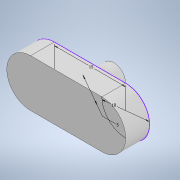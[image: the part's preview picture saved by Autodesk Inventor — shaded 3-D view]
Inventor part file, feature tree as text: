
AUTODESK INVENTOR PART (.ipt)
format: ipt  version: 2022 (Build 260153000, 153)  size: 107,008 bytes
history: native  units: mm
features: extrude x2, sketch x1
ambient origin geometry x8: Origin, YZ Plane, XZ Plane, XY Plane, X Axis, Y Axis, Z Axis, Center Point
bodies: Body1 (feature_tree)
feature tree (3):
  sketch  "Sketch1"  dims[d0=10.0mm d1=5.0mm d7=5.0mm d8=0.0mm d9=5.0mm d10=0.0mm d11=15.0mm]
  extrude  "Extrusion3"  Depth=5.0mm
  extrude  "Extrusion4"  Depth=5.0mm TaperAngle=0.0deg
